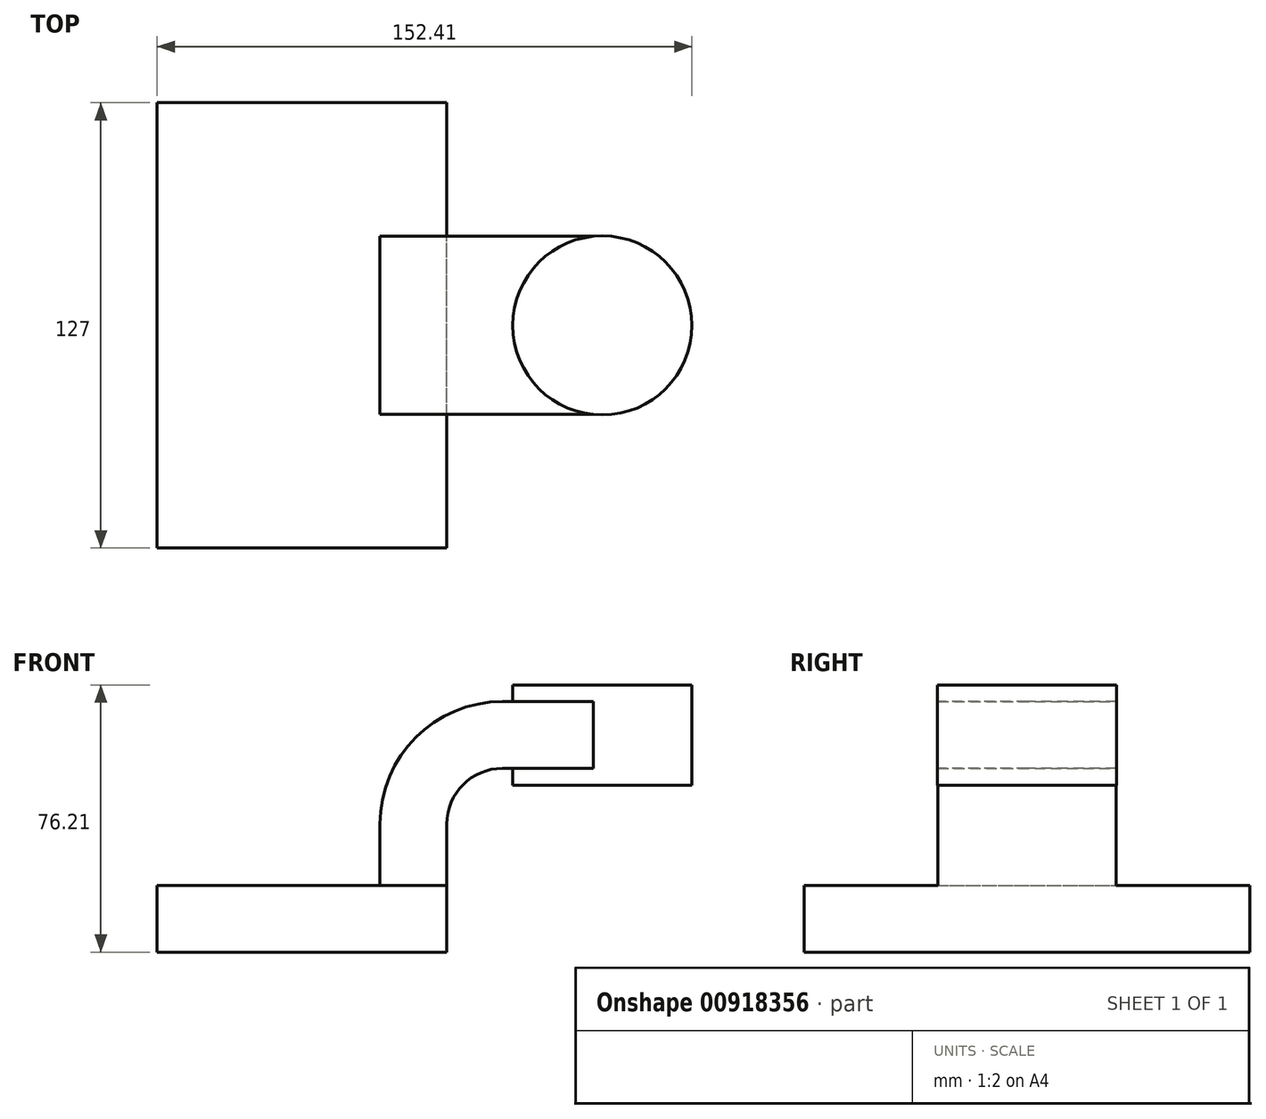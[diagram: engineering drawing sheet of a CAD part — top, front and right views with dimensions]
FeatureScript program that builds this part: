
annotation { "Feature Type Name" : "Feature", "Feature Type Description" : "" }
export const myFeature = defineFeature(function(context is Context, id is Id, definition is map)
    precondition{}
    {
        {
            var Q0;
            Q0=qCreatedBy(makeId("Front.planeOp"),FACE);
            var sketch = newSketch(context, id + "F0", { "sketchPlane" : qUnion([Q0])});
            skLineSegment(sketch, "E0.bottom", {"start": v(-41.28, -9.53) * mm, "end": v(41.28, -9.53) * mm});
            skLineSegment(sketch, "E0.top", {"start": v(-41.28, 9.53) * mm, "end": v(41.28, 9.53) * mm});
            skLineSegment(sketch, "E0.left", {"start": v(-41.28, -9.53) * mm, "end": v(-41.28, 9.53) * mm});
            skLineSegment(sketch, "E0.right", {"start": v(41.28, -9.53) * mm, "end": v(41.28, 9.53) * mm});
            skPoint(sketch, "E0.middle", {"position": v(0, 0) * mm});
            skLineSegment(sketch, "E1.bottom", {"start": v(60.33, 38.1) * mm, "end": v(111.13, 38.1) * mm});
            skLineSegment(sketch, "E1.top", {"start": v(60.33, 66.67) * mm, "end": v(111.13, 66.67) * mm});
            skLineSegment(sketch, "E1.left", {"start": v(60.33, 38.1) * mm, "end": v(60.33, 66.67) * mm});
            skLineSegment(sketch, "E1.right", {"start": v(111.13, 38.1) * mm, "end": v(111.13, 66.67) * mm});
            skPoint(sketch, "E1.middle", {"position": v(85.73, 52.39) * mm});
            skLineSegment(sketch, "E2", {"start": v(41.28, 9.53) * mm, "end": v(41.28, 27) * mm});
            skArc(sketch, "E3", {"start": v(41.27, 27) * mm, "mid": v(45.92, 38.23) * mm, "end": v(57.15, 42.88) * mm});
            skLineSegment(sketch, "E4", {"start": v(57.15, 42.88) * mm, "end": v(85.6, 42.88) * mm});
            skLineSegment(sketch, "E5.0", {"start": v(57.15, 61.93) * mm, "end": v(85.6, 61.93) * mm});
            skArc(sketch, "E5.1", {"start": v(22.23, 27) * mm, "mid": v(32.45, 51.7) * mm, "end": v(57.15, 61.93) * mm});
            skLineSegment(sketch, "E5.2", {"start": v(22.23, 9.53) * mm, "end": v(22.23, 27) * mm});
            skLineSegment(sketch, "E6", {"start": v(85.6, 38.1) * mm, "end": v(85.6, 66.67) * mm});
            skPoint(sketch, "E6.startSnap0", {"position": v(85.73, 38.1) * mm});
            skFitSpline(sketch, "E7", {"points": [v(-41.28, 9.53) * mm, v(57.15, 61.93) * mm], "startDerivative": vector(0.3, 75.1) * mm, "endDerivative": vector(144.17, -2.6) * mm});
            skSolve(sketch);
        }
        {
            var Q0;
            Q0=makeQuery(id+"F0.imprint","IMPRINT",FACE,{"disambiguationData":[TD([[makeQuery(id+"F0.imprint","IMPRINT",EDGE,{"derivedFrom":sQuery(id+"F0.wireOp",EDGE,"E0.bottom")}),1.0]])]});
            extrude(context, id + "F1", {"entities" : qUnion([Q0]), "endBound" : BoundingType.SYMMETRIC, "depth" : 127 * mm, "offsetDistance" : 25.4 * mm});
        }
        {
            var Q0;
            {var subQ5=sQuery(id+"F0.wireOp",EDGE,"E2");Q0=makeQuery(id+"F0.imprint","IMPRINT",FACE,{"disambiguationData":[TD([[makeQuery(id+"F0.imprint","IMPRINT",EDGE,{"derivedFrom":subQ5}),1.0]])]});}
            var Q1;
            {var subQ0=sQuery(id+"F0.wireOp",EDGE,"E4");var subQ1=sQuery(id+"F0.wireOp",EDGE,"E1.left");var subQ2=makeQuery(id+"F0.imprint","INTERSECT",VERTEX,{"derivedFrom":[subQ1,subQ0]});Q1=makeQuery(id+"F0.imprint","IMPRINT",FACE,{"disambiguationData":[TD([[makeQuery(id+"F0.imprint","IMPRINT",EDGE,{"disambiguationData":[TD([[subQ2,-1.0]])],"derivedFrom":subQ1}),-1.0]])]});}
            extrude(context, id + "F2", {"entities" : qUnion([Q0, Q1]), "operationType" : NewBodyOperationType.ADD, "endBound" : BoundingType.SYMMETRIC, "depth" : 50.8 * mm, "offsetDistance" : 25.4 * mm});
        }
        {
            var Q0;
            {var subQ4=sQuery(id+"F0.wireOp",EDGE,"E5.1");Q0=makeQuery(id+"F0.imprint","IMPRINT",FACE,{"disambiguationData":[TD([[makeQuery(id+"F0.imprint","IMPRINT",EDGE,{"derivedFrom":subQ4}),1.0]])]});}
            extrude(context, id + "F3", {"entities" : qUnion([Q0]), "operationType" : NewBodyOperationType.ADD, "endBound" : BoundingType.SYMMETRIC, "depth" : 15.88 * mm, "offsetDistance" : 25.4 * mm});
        }
        {
            var Q0;
            {var subQ0=sQuery(id+"F0.wireOp",EDGE,"E1.right");Q0=makeQuery(id+"F0.imprint","IMPRINT",FACE,{"disambiguationData":[TD([[makeQuery(id+"F0.imprint","IMPRINT",EDGE,{"derivedFrom":subQ0}),1.0]])]});}
            var Q1;
            Q1=sQuery(id+"F0.wireOp",EDGE,"E6");
            revolve(context, id + "F4", {"operationType" : NewBodyOperationType.ADD, "surfaceOperationType" : NewSurfaceOperationType.NEW, "entities" : qUnion([Q0]), "axis" : qUnion([Q1]), "revolveType" : RevolveType.FULL});
        }
    });
